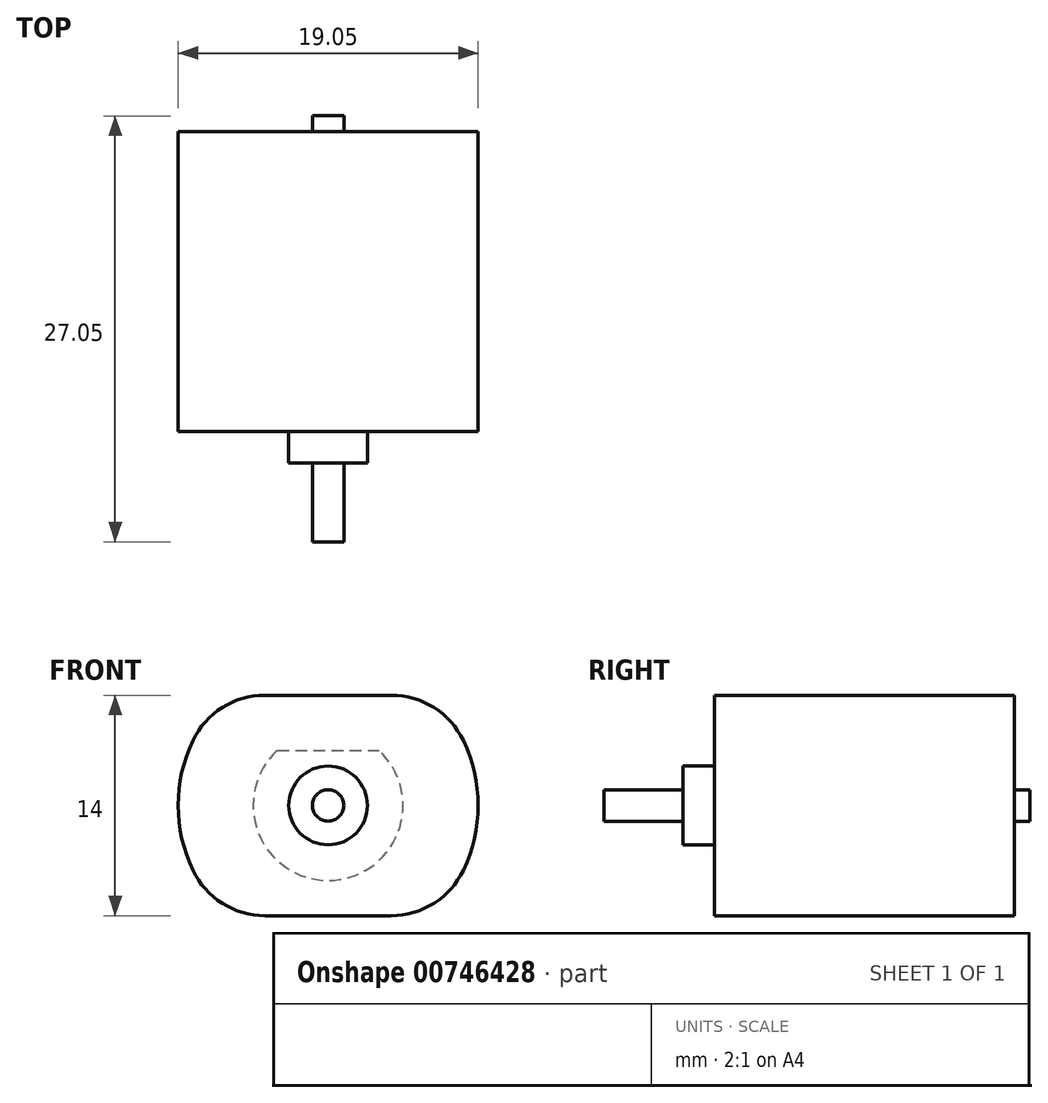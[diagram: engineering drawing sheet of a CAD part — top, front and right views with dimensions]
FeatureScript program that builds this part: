
annotation { "Feature Type Name" : "Feature", "Feature Type Description" : "" }
export const myFeature = defineFeature(function(context is Context, id is Id, definition is map)
    precondition{}
    {
        {
            var Q0;
            Q0=qCreatedBy(makeId("Top.planeOp"),FACE);
            var sketch = newSketch(context, id + "F0", { "sketchPlane" : qUnion([Q0])});
            skArc(sketch, "E0", {"start": v(-6.46, 7) * mm, "mid": v(-9.53, 0) * mm, "end": v(-6.46, -7) * mm});
            skPoint(sketch, "E1", {"position": v(0, 7) * mm});
            skLineSegment(sketch, "E2", {"start": v(0, 7) * mm, "end": v(-6.46, 7) * mm});
            skLineSegment(sketch, "E3", {"start": v(-6.46, 7) * mm, "end": v(6.46, 7) * mm});
            skLineSegment(sketch, "E4.MirrorCS", {"start": v(-6.46, -7) * mm, "end": v(6.46, -7) * mm});
            skArc(sketch, "E5.trimOffspring", {"start": v(6.46, -7) * mm, "mid": v(9.53, 0) * mm, "end": v(6.46, 7) * mm});
            skSolve(sketch);
        }
        {
            var Q0;
            Q0 = qSketchRegion(id + "F0", true);
            extrude(context, id + "F1", {"entities" : qUnion([Q0]), "depth" : 19.05 * mm, "offsetDistance" : 25.4 * mm});
        }
        {
            var Q0;
            Q0=makeQuery(id+"F1.opExtrude","SWEPT_EDGE",EDGE,{"disambiguationData":[OSD([sQuery(id+"F0.wireOp",EDGE,"E0"),sQuery(id+"F0.wireOp",EDGE,"E4.MirrorCS")])]});
            var Q1;
            Q1=makeQuery(id+"F1.opExtrude","SWEPT_EDGE",EDGE,{"disambiguationData":[OSD([sQuery(id+"F0.wireOp",EDGE,"E4.MirrorCS"),sQuery(id+"F0.wireOp",EDGE,"E5.trimOffspring")])]});
            var Q2;
            Q2=makeQuery(id+"F1.opExtrude","SWEPT_EDGE",EDGE,{"disambiguationData":[OSD([sQuery(id+"F0.wireOp",EDGE,"E0"),sQuery(id+"F0.wireOp",EDGE,"E3")])]});
            var Q3;
            Q3=makeQuery(id+"F1.opExtrude","SWEPT_EDGE",EDGE,{"disambiguationData":[OSD([sQuery(id+"F0.wireOp",EDGE,"E3"),sQuery(id+"F0.wireOp",EDGE,"E5.trimOffspring")])]});
            fillet(context, id + "F2", {"entities" : qUnion([Q0, Q1, Q2, Q3]), "radius" : 5.08 * mm, "tangentPropagation" : true, "allowEdgeOverflow" : false});
        }
        {
            var Q0;
            Q0=makeQuery(id+"F1.opExtrude","CAP_FACE",FACE,{"disambiguationData":[OSD([sQuery(id+"F0.wireOp",EDGE,"E0"),sQuery(id+"F0.wireOp",EDGE,"E3"),sQuery(id+"F0.wireOp",EDGE,"E4.MirrorCS"),sQuery(id+"F0.wireOp",EDGE,"E5.trimOffspring")])],"isStart":false});
            var sketch = newSketch(context, id + "F3", { "sketchPlane" : qUnion([Q0])});
            skCircle(sketch, "E6", {"center": v(0, 0) * mm, "radius": 2.5 * mm});
            skSolve(sketch);
        }
        {
            var Q0;
            Q0 = qSketchRegion(id + "F3", true);
            extrude(context, id + "F4", {"entities" : qUnion([Q0]), "operationType" : NewBodyOperationType.ADD, "depth" : 2 * mm, "offsetDistance" : 25.4 * mm});
        }
        {
            var Q0;
            Q0=makeQuery(id+"F4.opExtrude","CAP_FACE",FACE,{"disambiguationData":[OSD([sQuery(id+"F3.wireOp",EDGE,"E6")])],"isStart":false});
            var sketch = newSketch(context, id + "F5", { "sketchPlane" : qUnion([Q0])});
            skCircle(sketch, "E7", {"center": v(0, 0) * mm, "radius": 1 * mm});
            skSolve(sketch);
        }
        {
            var Q0;
            Q0 = qSketchRegion(id + "F5", true);
            extrude(context, id + "F6", {"entities" : qUnion([Q0]), "operationType" : NewBodyOperationType.ADD, "depth" : 5 * mm, "offsetDistance" : 25.4 * mm});
        }
        {
            var Q0;
            Q0=makeQuery(id+"F1.opExtrude","CAP_FACE",FACE,{"disambiguationData":[OSD([sQuery(id+"F0.wireOp",EDGE,"E0"),sQuery(id+"F0.wireOp",EDGE,"E3"),sQuery(id+"F0.wireOp",EDGE,"E4.MirrorCS"),sQuery(id+"F0.wireOp",EDGE,"E5.trimOffspring")])],"isStart":true});
            var sketch = newSketch(context, id + "F7", { "sketchPlane" : qUnion([Q0])});
            skArc(sketch, "E8", {"start": v(3.23, -3.5) * mm, "mid": v(0, 4.76) * mm, "end": v(-3.23, -3.5) * mm});
            skPoint(sketch, "E9", {"position": v(0, -3.5) * mm});
            skLineSegment(sketch, "E10", {"start": v(0, -3.5) * mm, "end": v(3.23, -3.5) * mm});
            skLineSegment(sketch, "E11", {"start": v(3.23, -3.5) * mm, "end": v(-3.23, -3.5) * mm});
            skSolve(sketch);
        }
        {
            var Q0;
            Q0 = qSketchRegion(id + "F7", true);
            extrude(context, id + "F8", {"entities" : qUnion([Q0]), "operationType" : NewBodyOperationType.ADD, "depth" : 1 / 203.2 * mm, "offsetDistance" : 25.4 * mm});
        }
        {
            var Q0;
            Q0=makeQuery(id+"F8.opExtrude","CAP_FACE",FACE,{"disambiguationData":[OSD([sQuery(id+"F7.wireOp",EDGE,"E8"),sQuery(id+"F7.wireOp",EDGE,"E11")])],"isStart":false});
            var sketch = newSketch(context, id + "F9", { "sketchPlane" : qUnion([Q0])});
            skCircle(sketch, "E12", {"center": v(0, 0) * mm, "radius": 1 * mm});
            skSolve(sketch);
        }
        {
            var Q0;
            Q0 = qSketchRegion(id + "F9", true);
            extrude(context, id + "F10", {"entities" : qUnion([Q0]), "operationType" : NewBodyOperationType.ADD, "depth" : 1 * mm, "offsetDistance" : 25.4 * mm});
        }
        {
            var Q0;
            Q0=qCreatedBy(makeId("Top.planeOp"),FACE);
            var sketch = newSketch(context, id + "F11", { "sketchPlane" : qUnion([Q0])});
            skLineSegment(sketch, "E13", {"start": v(-38.2, 0) * mm, "end": v(42, 0) * mm});
            skSolve(sketch);
        }
        {
            var Q0;
            Q0=makeQuery(id+"F1.opExtrude","SWEPT_BODY",BODY,{"disambiguationData":[OSD([sQuery(id+"F0.wireOp",EDGE,"E0"),sQuery(id+"F0.wireOp",EDGE,"E3"),sQuery(id+"F0.wireOp",EDGE,"E4.MirrorCS"),sQuery(id+"F0.wireOp",EDGE,"E5.trimOffspring")])]});
            var Q1;
            Q1=sQuery(id+"F11.wireOp",EDGE,"E13");
            transform(context, id + "F12", {"entities" : qUnion([Q0]), "transformType" : TransformType.ROTATION, "transformAxis" : qUnion([Q1]), "angle" : 90 * degree, "makeCopy" : false});
        }
    });
